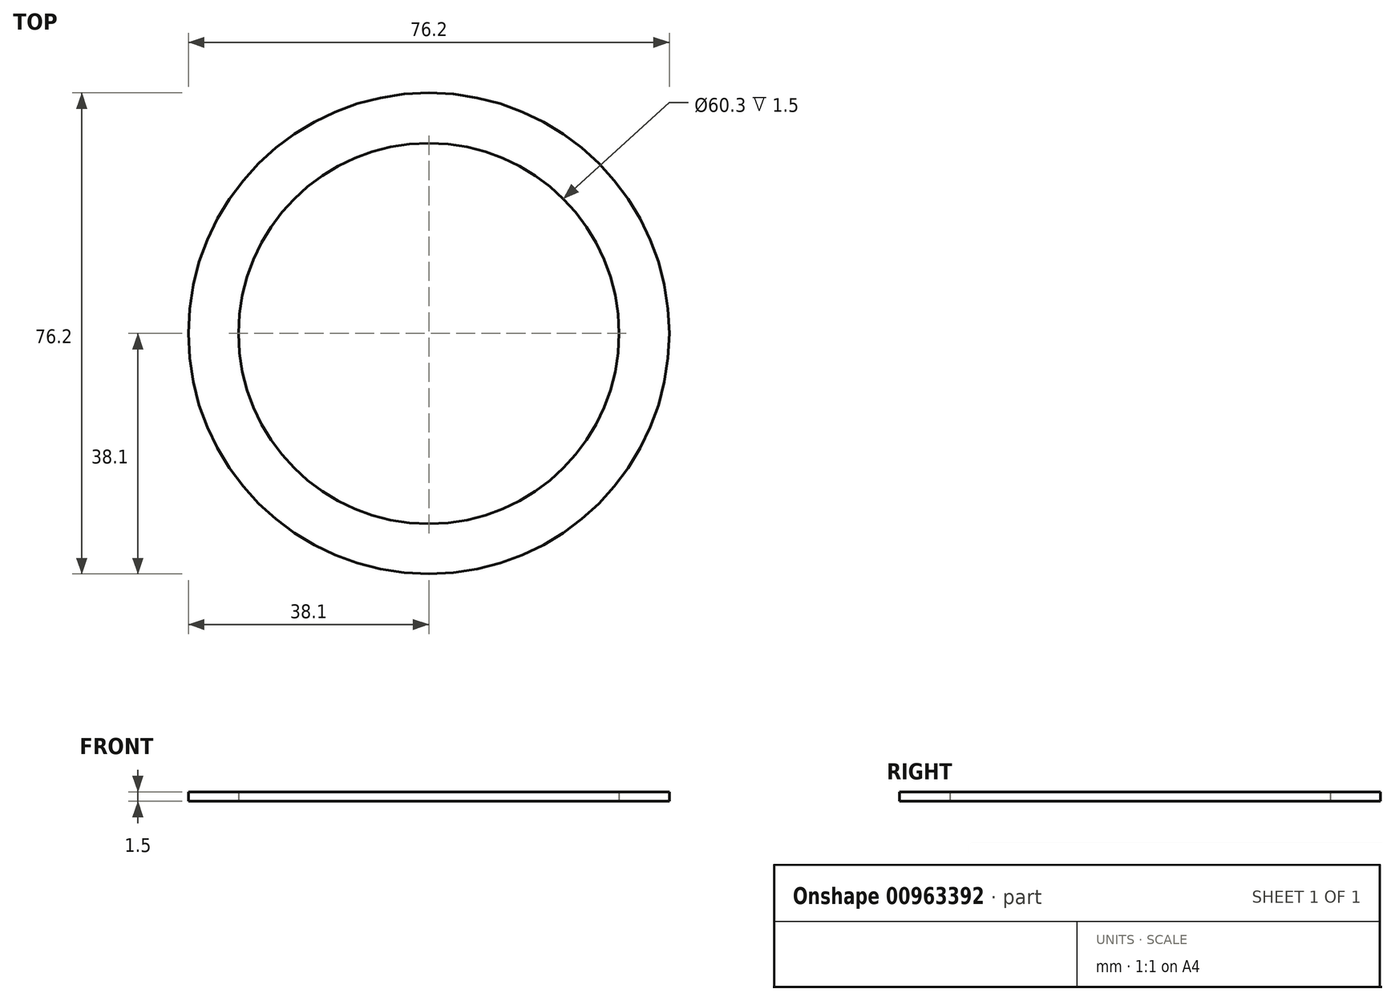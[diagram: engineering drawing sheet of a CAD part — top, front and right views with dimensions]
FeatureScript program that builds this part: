
annotation { "Feature Type Name" : "Feature", "Feature Type Description" : "" }
export const myFeature = defineFeature(function(context is Context, id is Id, definition is map)
    precondition{}
    {
        {
            var Q0;
            Q0=qCreatedBy(makeId("Top.planeOp"),FACE);
            var sketch = newSketch(context, id + "F0", { "sketchPlane" : qUnion([Q0])});
            skCircle(sketch, "E0", {"center": v(0, 0) * mm, "radius": 38.1 * mm});
            skCircle(sketch, "E1", {"center": v(0, 0) * mm, "radius": 30.15 * mm});
            skSolve(sketch);
        }
        {
            var Q0;
            Q0=makeQuery(id+"F0.imprint","IMPRINT",FACE,{"disambiguationData":[TD([[makeQuery(id+"F0.imprint","IMPRINT",EDGE,{"derivedFrom":sQuery(id+"F0.wireOp",EDGE,"E0")}),1.0]])]});
            extrude(context, id + "F1", {"entities" : qUnion([Q0]), "depth" : 1.5 * mm, "offsetDistance" : 25 * mm});
        }
    });
